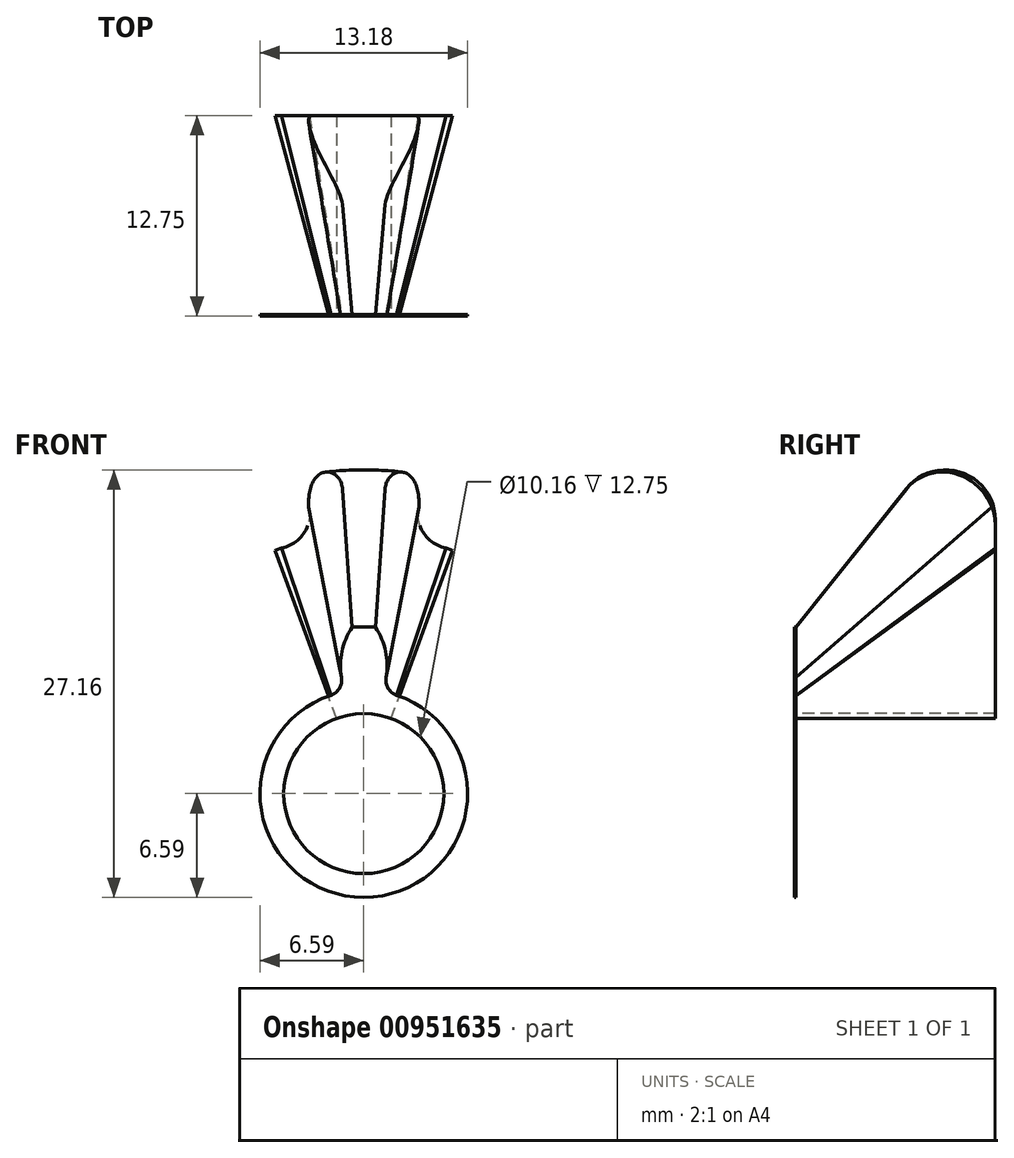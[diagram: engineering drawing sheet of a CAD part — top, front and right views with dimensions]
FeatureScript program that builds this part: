
annotation { "Feature Type Name" : "Feature", "Feature Type Description" : "" }
export const myFeature = defineFeature(function(context is Context, id is Id, definition is map)
    precondition{}
    {
        {
            var Q0;
            Q0=qCreatedBy(makeId("Front.planeOp"),FACE);
            cPlane(context, id + "F0", {"entities" : qUnion([Q0]), "cplaneType" : CPlaneType.OFFSET, "offset" : 12.7 * mm, "oppositeDirection" : true, "width" : 152.4 * mm, "height" : 152.4 * mm});
        }
        {
            assignVariable(context, id + "F1", {"name" : "GearThickness", "anyValue" : .1});
        }
        {
            var Q0;
            Q0=qCreatedBy(makeId("Front.planeOp"),FACE);
            var sketch = newSketch(context, id + "F2", { "sketchPlane" : qUnion([Q0])});
            skCircle(sketch, "E0", {"center": v(0, 0) * mm, "radius": 6.6 * mm});
            skSolve(sketch);
        }
        {
            var Q0;
            Q0=qSketchRegion(id+"F2",true);
            extrude(context, id + "F3", {"entities" : qUnion([Q0]), "endBound" : BoundingType.SYMMETRIC, "offsetDistance" : 25 * mm, "depth" : (getVariable(context, 'GearThickness')) * mm});
        }
        {
            var Q0;
            Q0=qCreatedBy(makeId("Front.planeOp"),FACE);
            var sketch = newSketch(context, id + "F4", { "sketchPlane" : qUnion([Q0])});
            skCircle(sketch, "E1", {"center": v(0, 0) * mm, "radius": 8.6 * mm, "construction": true});
            skLineSegment(sketch, "E2", {"start": v(0, 28.09) * mm, "end": v(0, 0) * mm, "construction": true});
            skLineSegment(sketch, "E3", {"start": v(0, 0) * mm, "end": v(-1.47, 8.46) * mm, "construction": true});
            skLineSegment(sketch, "E4", {"start": v(0, 0) * mm, "end": v(1.47, 8.46) * mm, "construction": true});
            skCircle(sketch, "E5", {"center": v(0, 0) * mm, "radius": 10.6 * mm, "construction": true});
            skArc(sketch, "E6", {"start": v(1.18, 6.48) * mm, "mid": v(0, 6.6) * mm, "end": v(-1.18, 6.48) * mm});
            skArc(sketch, "E7", {"start": v(0.74, 10.56) * mm, "mid": v(0, 10.6) * mm, "end": v(-0.74, 10.56) * mm});
            skLineSegment(sketch, "E8", {"start": v(-1.47, 8.46) * mm, "end": v(-0.72, 17.69) * mm, "construction": true});
            skLineSegment(sketch, "E9", {"start": v(-1.47, 8.46) * mm, "end": v(-0.74, 10.56) * mm, "construction": true});
            skArc(sketch, "E10", {"start": v(-0.74, 10.56) * mm, "mid": v(-1.46, 8.58) * mm, "end": v(-1.18, 6.48) * mm});
            skArc(sketch, "E11", {"start": v(1.18, 6.48) * mm, "mid": v(1.46, 8.58) * mm, "end": v(0.74, 10.56) * mm});
            skSolve(sketch);
        }
        {
            var Q0;
            Q0=qSketchRegion(id+"F4",true);
            extrude(context, id + "F5", {"entities" : qUnion([Q0]), "endBound" : BoundingType.SYMMETRIC, "depth" : (getVariable(context, 'GearThickness')) * mm});
        }
        {
            var Q0;
            Q0=qCreatedBy(makeId("Front.planeOp"),FACE);
            var sketch = newSketch(context, id + "F6", { "sketchPlane" : qUnion([Q0])});
            skArc(sketch, "E12", {"start": v(1.42, 7.36) * mm, "mid": v(1.55, 6.68) * mm, "end": v(2.1, 6.25) * mm});
            skArc(sketch, "E13", {"start": v(-2.1, 6.25) * mm, "mid": v(-1.55, 6.68) * mm, "end": v(-1.42, 7.36) * mm});
            skArc(sketch, "E14", {"start": v(2.1, 6.25) * mm, "mid": v(0, 6.6) * mm, "end": v(-2.1, 6.25) * mm});
            skLineSegment(sketch, "E15", {"start": v(-1.42, 7.36) * mm, "end": v(1.42, 7.36) * mm});
            skSolve(sketch);
        }
        {
            var Q0;
            Q0=qSketchRegion(id+"F6",true);
            extrude(context, id + "F7", {"entities" : qUnion([Q0]), "operationType" : NewBodyOperationType.ADD, "endBound" : BoundingType.SYMMETRIC, "depth" : (getVariable(context, 'GearThickness')) * mm});
        }
        {
            var Q0;
            Q0=makeQuery(id+"F3.opExtrude","CAP_FACE",FACE,{"disambiguationData":[OSD([sQuery(id+"F2.wireOp",EDGE,"E0")])],"isStart":true});
            var sketch = newSketch(context, id + "F8", { "sketchPlane" : qUnion([Q0])});
            skLineSegment(sketch, "E16", {"start": v(0, 0) * mm, "end": v(-2.1, 6.25) * mm, "construction": true});
            skLineSegment(sketch, "E17", {"start": v(0, 0) * mm, "end": v(-1.42, 7.36) * mm, "construction": true});
            skLineSegment(sketch, "E18", {"start": v(0, 0) * mm, "end": v(-0.74, 10.56) * mm, "construction": true});
            skLineSegment(sketch, "E19", {"start": v(0, 0) * mm, "end": v(0.74, 10.56) * mm, "construction": true});
            skLineSegment(sketch, "E20", {"start": v(0, 0) * mm, "end": v(1.42, 7.36) * mm, "construction": true});
            skLineSegment(sketch, "E21", {"start": v(0, 0) * mm, "end": v(2.1, 6.25) * mm, "construction": true});
            skSolve(sketch);
        }
        {
            var Q0;
            Q0=qCreatedBy(makeId("Top.planeOp"),FACE);
            var sketch = newSketch(context, id + "F9", { "sketchPlane" : qUnion([Q0])});
            skLineSegment(sketch, "E22", {"start": v(0, 0) * mm, "end": v(0, 9.45) * mm});
            skSolve(sketch);
        }
        {
            var Q0;
            Q0=sQuery(id+"F9.wireOp",VERTEX,"E22.end");
            var Q1;
            Q1=sQuery(id+"F9.wireOp",VERTEX,"E22.start");
            var Q2;
            Q2=sQuery(id+"F8.wireOp",VERTEX,"E16.end");
            cPlane(context, id + "F10", {"entities" : qUnion([Q0, Q1, Q2]), "cplaneType" : CPlaneType.THREE_POINT, "offset" : 25.4 * mm, "width" : 152.4 * mm, "height" : 152.4 * mm});
        }
        {
            var Q0;
            Q0=qCreatedBy(id+"F10.planeOp",FACE);
            var sketch = newSketch(context, id + "F11", { "sketchPlane" : qUnion([Q0])});
            skLineSegment(sketch, "E23", {"start": v(0.05, 6.59) * mm, "end": v(12.7, 19.24) * mm});
            skSolve(sketch);
        }
        {
            var Q0;
            Q0=sQuery(id+"F8.wireOp",VERTEX,"E20.start");
            var Q1;
            Q1=sQuery(id+"F9.wireOp",VERTEX,"E22.end");
            var Q2;
            Q2=sQuery(id+"F8.wireOp",VERTEX,"E17.end");
            cPlane(context, id + "F12", {"entities" : qUnion([Q0, Q1, Q2]), "cplaneType" : CPlaneType.THREE_POINT, "offset" : 25.4 * mm, "width" : 152.4 * mm, "height" : 152.4 * mm});
        }
        {
            var Q0;
            Q0=qCreatedBy(id+"F12.planeOp",FACE);
            var sketch = newSketch(context, id + "F13", { "sketchPlane" : qUnion([Q0])});
            skLineSegment(sketch, "E24", {"start": v(-0.05, 7.5) * mm, "end": v(-12.7, 20.15) * mm});
            skSolve(sketch);
        }
        {
            var Q0;
            Q0=sQuery(id+"F8.wireOp",VERTEX,"E18.end");
            var Q1;
            Q1=sQuery(id+"F9.wireOp",VERTEX,"E22.end");
            var Q2;
            Q2=sQuery(id+"F9.wireOp",VERTEX,"E22.start");
            cPlane(context, id + "F14", {"entities" : qUnion([Q0, Q1, Q2]), "cplaneType" : CPlaneType.THREE_POINT, "offset" : 25.4 * mm, "width" : 152.4 * mm, "height" : 152.4 * mm});
        }
        {
            var Q0;
            Q0=qCreatedBy(id+"F14.planeOp",FACE);
            var sketch = newSketch(context, id + "F15", { "sketchPlane" : qUnion([Q0])});
            skLineSegment(sketch, "E25", {"start": v(0.05, 10.59) * mm, "end": v(12.7, 23.24) * mm});
            skSolve(sketch);
        }
        {
            var Q0;
            Q0=sQuery(id+"F8.wireOp",VERTEX,"E20.start");
            var Q1;
            Q1=sQuery(id+"F8.wireOp",VERTEX,"E19.end");
            var Q2;
            Q2=sQuery(id+"F9.wireOp",VERTEX,"E22.end");
            cPlane(context, id + "F16", {"entities" : qUnion([Q0, Q1, Q2]), "cplaneType" : CPlaneType.THREE_POINT, "offset" : 25.4 * mm, "width" : 152.4 * mm, "height" : 152.4 * mm});
        }
        {
            var Q0;
            Q0=qCreatedBy(id+"F16.planeOp",FACE);
            var sketch = newSketch(context, id + "F17", { "sketchPlane" : qUnion([Q0])});
            skLineSegment(sketch, "E26", {"start": v(0.05, 10.59) * mm, "end": v(12.7, 23.24) * mm});
            skSolve(sketch);
        }
        {
            var Q0;
            Q0=sQuery(id+"F9.wireOp",VERTEX,"E22.end");
            var Q1;
            Q1=sQuery(id+"F9.wireOp",VERTEX,"E22.start");
            var Q2;
            Q2=sQuery(id+"F8.wireOp",VERTEX,"E20.end");
            cPlane(context, id + "F18", {"entities" : qUnion([Q0, Q1, Q2]), "cplaneType" : CPlaneType.THREE_POINT, "offset" : 25.4 * mm, "width" : 152.4 * mm, "height" : 152.4 * mm});
        }
        {
            var Q0;
            Q0=qCreatedBy(id+"F18.planeOp",FACE);
            var sketch = newSketch(context, id + "F19", { "sketchPlane" : qUnion([Q0])});
            skLineSegment(sketch, "E27", {"start": v(0.05, 7.5) * mm, "end": v(12.7, 20.15) * mm});
            skSolve(sketch);
        }
        {
            var Q0;
            Q0=sQuery(id+"F9.wireOp",VERTEX,"E22.end");
            var Q1;
            Q1=sQuery(id+"F8.wireOp",VERTEX,"E21.end");
            var Q2;
            Q2=sQuery(id+"F9.wireOp",VERTEX,"E22.start");
            cPlane(context, id + "F20", {"entities" : qUnion([Q0, Q1, Q2]), "cplaneType" : CPlaneType.THREE_POINT, "offset" : 25.4 * mm, "width" : 152.4 * mm, "height" : 152.4 * mm});
        }
        {
            var Q0;
            Q0=qCreatedBy(id+"F20.planeOp",FACE);
            var sketch = newSketch(context, id + "F21", { "sketchPlane" : qUnion([Q0])});
            skLineSegment(sketch, "E28", {"start": v(-0.05, 6.6) * mm, "end": v(-12.7, 19.24) * mm});
            skSolve(sketch);
        }
        {
            var Q0;
            Q0=qCreatedBy(id+"F0.planeOp",FACE);
            var sketch = newSketch(context, id + "F22", { "sketchPlane" : qUnion([Q0])});
            skArc(sketch, "E29", {"start": v(1.85, 26.41) * mm, "mid": v(0, 26.48) * mm, "end": v(-1.85, 26.41) * mm});
            skArc(sketch, "E30", {"start": v(-1.85, 26.41) * mm, "mid": v(-3.25, 22.52) * mm, "end": v(-3.55, 18.4) * mm});
            skArc(sketch, "E31", {"start": v(3.55, 18.4) * mm, "mid": v(3.25, 22.52) * mm, "end": v(1.85, 26.41) * mm});
            skArc(sketch, "E32", {"start": v(-5.22, 15.6) * mm, "mid": v(-3.75, 16.62) * mm, "end": v(-3.55, 18.4) * mm});
            skArc(sketch, "E33", {"start": v(3.55, 18.4) * mm, "mid": v(3.75, 16.62) * mm, "end": v(5.22, 15.6) * mm});
            skLineSegment(sketch, "E34", {"start": v(0, 0) * mm, "end": v(-5.22, 15.6) * mm, "construction": true});
            skLineSegment(sketch, "E35", {"start": v(0, 0) * mm, "end": v(-3.55, 18.4) * mm, "construction": true});
            skLineSegment(sketch, "E36", {"start": v(0, 0) * mm, "end": v(-1.85, 26.41) * mm, "construction": true});
            skLineSegment(sketch, "E37", {"start": v(0, 0) * mm, "end": v(1.85, 26.41) * mm, "construction": true});
            skLineSegment(sketch, "E38", {"start": v(0, 0) * mm, "end": v(3.55, 18.4) * mm, "construction": true});
            skLineSegment(sketch, "E39", {"start": v(0, 0) * mm, "end": v(5.22, 15.6) * mm, "construction": true});
            skLineSegment(sketch, "E40", {"start": v(0, 0) * mm, "end": v(5.63, 15.45) * mm});
            skLineSegment(sketch, "E41", {"start": v(0, 0) * mm, "end": v(-5.63, 15.45) * mm});
            skLineSegment(sketch, "E42", {"start": v(0, 0) * mm, "end": v(0, 20.32) * mm, "construction": true});
            skArc(sketch, "E43", {"start": v(-5.22, 15.6) * mm, "mid": v(-5.42, 15.53) * mm, "end": v(-5.63, 15.45) * mm});
            skArc(sketch, "E44", {"start": v(5.63, 15.45) * mm, "mid": v(5.42, 15.53) * mm, "end": v(5.22, 15.6) * mm});
            skSolve(sketch);
        }
        {
            var Q0;
            Q0=makeQuery(id+"F8.imprint","IMPRINT",FACE,{"disambiguationData":[TD([[makeQuery(id+"F8.imprint","IMPRINT",EDGE,{"derivedFrom":makeQuery(id+"F3.opExtrude","CAP_EDGE",EDGE,{"disambiguationData":[OSD([sQuery(id+"F2.wireOp",EDGE,"E0")])],"isStart":true})}),-1.0]])]});
            var sketch = newSketch(context, id + "F23", { "sketchPlane" : qUnion([Q0])});
            skLineSegment(sketch, "E45", {"start": v(0, 0) * mm, "end": v(-2.1, 6.25) * mm, "construction": true});
            skLineSegment(sketch, "E46", {"start": v(0, 0) * mm, "end": v(2.1, 6.25) * mm, "construction": true});
            skArc(sketch, "E47.0", {"start": v(-1.42, 7.36) * mm, "mid": v(-1.55, 6.68) * mm, "end": v(-2.1, 6.25) * mm});
            skArc(sketch, "E47.1", {"start": v(2.1, 6.25) * mm, "mid": v(1.55, 6.68) * mm, "end": v(1.42, 7.36) * mm});
            skArc(sketch, "E47.2", {"start": v(0.74, 10.56) * mm, "mid": v(1.39, 9.03) * mm, "end": v(1.42, 7.36) * mm});
            skArc(sketch, "E47.3", {"start": v(-0.74, 10.56) * mm, "mid": v(0, 10.59) * mm, "end": v(0.74, 10.56) * mm});
            skArc(sketch, "E47.4", {"start": v(-1.42, 7.36) * mm, "mid": v(-1.39, 9.03) * mm, "end": v(-0.74, 10.56) * mm});
            skLineSegment(sketch, "E48", {"start": v(0, 0) * mm, "end": v(-2.25, 6.2) * mm});
            skLineSegment(sketch, "E49", {"start": v(0, 0) * mm, "end": v(2.25, 6.2) * mm});
            skLineSegment(sketch, "E50", {"start": v(0, 0) * mm, "end": v(0, 6.32) * mm});
            skArc(sketch, "E51", {"start": v(-2.1, 6.25) * mm, "mid": v(-2.17, 6.22) * mm, "end": v(-2.25, 6.2) * mm});
            skArc(sketch, "E52", {"start": v(2.25, 6.2) * mm, "mid": v(2.17, 6.22) * mm, "end": v(2.1, 6.25) * mm});
            skSolve(sketch);
        }
        {
            var Q0;
            Q0 = qSketchRegion(id + "F23", true);
            var Q1;
            Q1 = qSketchRegion(id + "F22", true);
            loft(context, id + "F24", {"operationType" : NewBodyOperationType.ADD, "sheetProfilesArray" : [{ "sheetProfileEntities" : qUnion([Q0]) }, { "sheetProfileEntities" : qUnion([Q1]) }]});
        }
        {
            var Q0;
            Q0=makeQuery(id+"F24.opLoft","MID_CAP_EDGE",EDGE,{"disambiguationData":[OSD([sQuery(id+"F22.wireOp",EDGE,"E29"),sQuery(id+"F22.wireOp",EDGE,"E30"),sQuery(id+"F22.wireOp",EDGE,"E31")])],"capPos":1.0});
            fillet(context, id + "F25", {"entities" : qUnion([Q0]), "radius" : 3.17 * mm, "tangentPropagation" : true, "allowEdgeOverflow" : false});
        }
        {
            var Q0;
            Q0=makeQuery(id+"F24.boolean.opBoolean","MERGE",FACE,{"derivedFrom":[makeQuery(id+"F3.opExtrude","CAP_FACE",FACE,{"disambiguationData":[OSD([sQuery(id+"F2.wireOp",EDGE,"E0")])],"isStart":false}),makeQuery(id+"F7.boolean.opBoolean","MERGE",FACE,{"derivedFrom":[makeQuery(id+"F5.opExtrude","CAP_FACE",FACE,{"disambiguationData":[OSD([sQuery(id+"F4.wireOp",EDGE,"E6"),sQuery(id+"F4.wireOp",EDGE,"E7"),sQuery(id+"F4.wireOp",EDGE,"E10"),sQuery(id+"F4.wireOp",EDGE,"E11")])],"isStart":false}),makeQuery(id+"F7.opExtrude","CAP_FACE",FACE,{"disambiguationData":[OSD([sQuery(id+"F6.wireOp",EDGE,"E12"),sQuery(id+"F6.wireOp",EDGE,"E13"),sQuery(id+"F6.wireOp",EDGE,"E14"),sQuery(id+"F6.wireOp",EDGE,"E15")])],"isStart":false})]})]});
            var sketch = newSketch(context, id + "F26", { "sketchPlane" : qUnion([Q0])});
            skCircle(sketch, "E53", {"center": v(0, 0) * mm, "radius": 5.08 * mm});
            skSolve(sketch);
        }
        {
            var Q0;
            Q0 = qSketchRegion(id + "F26", true);
            extrude(context, id + "F27", {"entities" : qUnion([Q0]), "operationType" : NewBodyOperationType.REMOVE, "endBound" : BoundingType.THROUGH_ALL, "oppositeDirection" : true, "depth" : 25.4 * mm, "offsetDistance" : 25.4 * mm});
        }
    });
